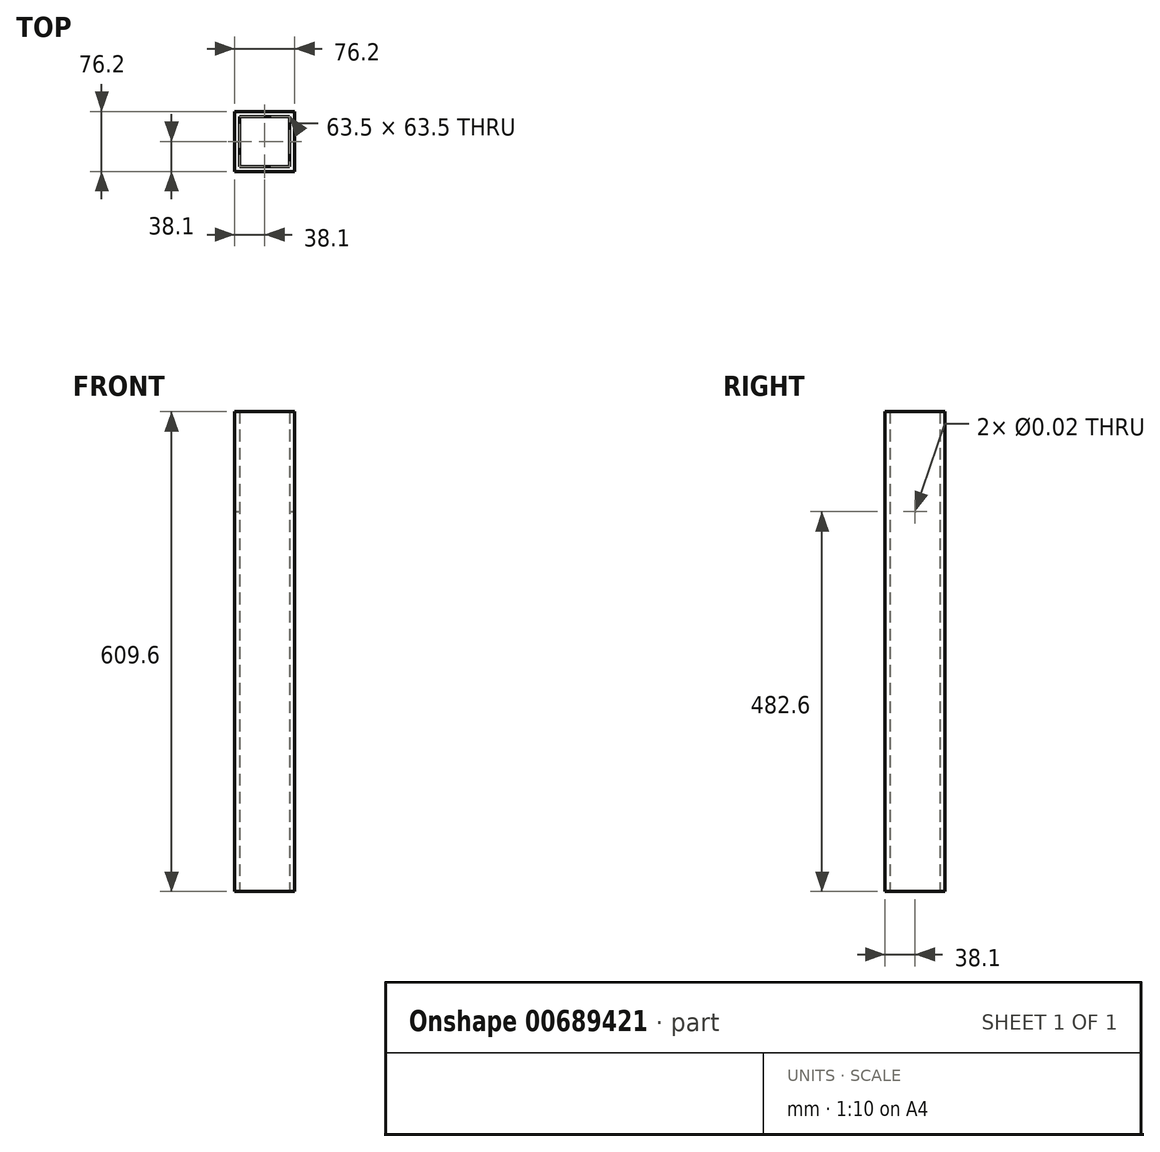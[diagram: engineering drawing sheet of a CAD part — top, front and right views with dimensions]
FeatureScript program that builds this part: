
annotation { "Feature Type Name" : "Feature", "Feature Type Description" : "" }
export const myFeature = defineFeature(function(context is Context, id is Id, definition is map)
    precondition{}
    {
        {
            var Q0;
            Q0=qCreatedBy(makeId("Top.planeOp"),FACE);
            var sketch = newSketch(context, id + "F0", { "sketchPlane" : qUnion([Q0])});
            skLineSegment(sketch, "E0.bottom", {"start": v(-38.1, 38.1) * mm, "end": v(38.1, 38.1) * mm});
            skLineSegment(sketch, "E0.top", {"start": v(-38.1, -38.1) * mm, "end": v(38.1, -38.1) * mm});
            skLineSegment(sketch, "E0.left", {"start": v(-38.1, 38.1) * mm, "end": v(-38.1, -38.1) * mm});
            skLineSegment(sketch, "E0.right", {"start": v(38.1, 38.1) * mm, "end": v(38.1, -38.1) * mm});
            skPoint(sketch, "E0.middle", {"position": v(0, 0) * mm});
            skLineSegment(sketch, "E1.bottom", {"start": v(-31.75, 31.75) * mm, "end": v(31.75, 31.75) * mm});
            skLineSegment(sketch, "E1.top", {"start": v(-31.75, -31.75) * mm, "end": v(31.75, -31.75) * mm});
            skLineSegment(sketch, "E1.left", {"start": v(-31.75, 31.75) * mm, "end": v(-31.75, -31.75) * mm});
            skLineSegment(sketch, "E1.right", {"start": v(31.75, 31.75) * mm, "end": v(31.75, -31.75) * mm});
            skSolve(sketch);
        }
        {
            var Q0;
            Q0=makeQuery(id+"F0.imprint","IMPRINT",FACE,{"disambiguationData":[TD([[makeQuery(id+"F0.imprint","IMPRINT",EDGE,{"derivedFrom":sQuery(id+"F0.wireOp",EDGE,"E0.bottom")}),-1.0]])]});
            extrude(context, id + "F1", {"entities" : qUnion([Q0]), "depth" : 609.6 * mm, "offsetDistance" : 25.4 * mm});
        }
        {
            var Q0;
            Q0=makeQuery(id+"F1.opExtrude","SWEPT_FACE",FACE,{"disambiguationData":[OSD([sQuery(id+"F0.wireOp",EDGE,"E0.right")])]});
            var sketch = newSketch(context, id + "F2", { "sketchPlane" : qUnion([Q0])});
            skPoint(sketch, "E2", {"position": v(0, 482.6) * mm});
            skSolve(sketch);
        }
        {
            var Q0;
            Q0=sQuery(id+"F2.wireOp",VERTEX,"E2");
            var Q1;
            Q1=makeQuery(id+"F1.opExtrude","SWEPT_BODY",BODY,{"disambiguationData":[OSD([sQuery(id+"F0.wireOp",EDGE,"E0.bottom"),sQuery(id+"F0.wireOp",EDGE,"E0.top"),sQuery(id+"F0.wireOp",EDGE,"E0.left"),sQuery(id+"F0.wireOp",EDGE,"E0.right"),sQuery(id+"F0.wireOp",EDGE,"E1.bottom"),sQuery(id+"F0.wireOp",EDGE,"E1.top"),sQuery(id+"F0.wireOp",EDGE,"E1.left"),sQuery(id+"F0.wireOp",EDGE,"E1.right")])]});
            hole(context, id + "F3", {"style" : HoleStyle.SIMPLE, "endStyle" : HoleEndStyle.THROUGH, "standardTappedOrClearance" : lookupTablePath({ "standard" : "ANSI", "size" : "1/2 (0.5)", "type" : "Drilled" }), "standardBlindInLast" : lookupTablePath({ "standard" : "ANSI", "size" : "1/2", "type" : "Drilled" }), "holeDiameter" : 1 / 50.8 * mm, "majorDiameter" : 22.22 * mm, "tappedDepth" : 10.3 * mm, "tapClearance" : 3, "locations" : qUnion([Q0]), "scope" : qUnion([Q1])});
        }
    });
